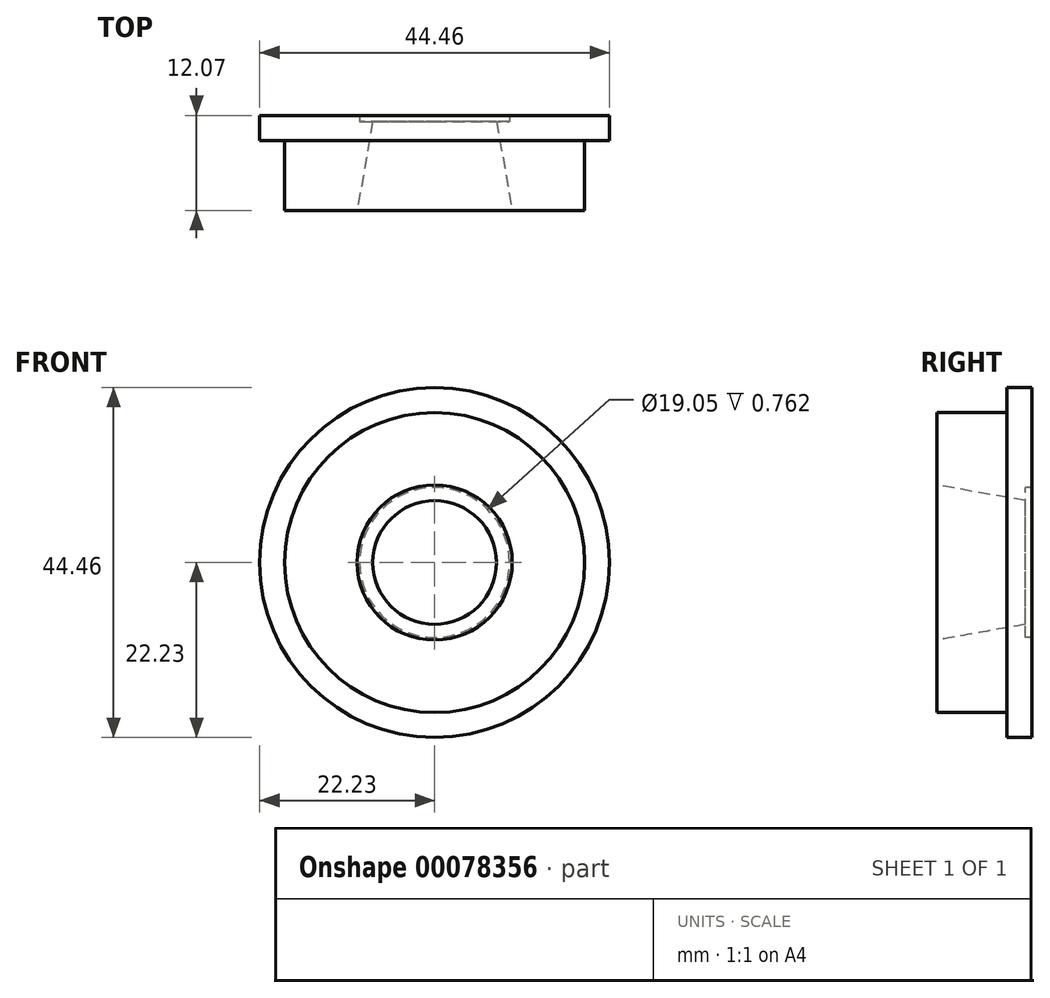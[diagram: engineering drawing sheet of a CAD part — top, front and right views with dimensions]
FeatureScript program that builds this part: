
annotation { "Feature Type Name" : "Feature", "Feature Type Description" : "" }
export const myFeature = defineFeature(function(context is Context, id is Id, definition is map)
    precondition{}
    {
        {
            var Q0;
            Q0=qCreatedBy(makeId("Right.planeOp"),FACE);
            var sketch = newSketch(context, id + "F0", { "sketchPlane" : qUnion([Q0])});
            skLineSegment(sketch, "E0", {"start": v(0, 9.85) * mm, "end": v(0, 19.05) * mm});
            skLineSegment(sketch, "E1", {"start": v(0, 19.05) * mm, "end": v(8.9, 19.05) * mm});
            skLineSegment(sketch, "E2", {"start": v(8.9, 19.05) * mm, "end": v(8.9, 22.23) * mm});
            skLineSegment(sketch, "E3", {"start": v(8.9, 22.23) * mm, "end": v(12.07, 22.23) * mm});
            skLineSegment(sketch, "E4", {"start": v(12.07, 22.23) * mm, "end": v(12.07, 9.53) * mm});
            skLineSegment(sketch, "E5", {"start": v(12.07, 9.53) * mm, "end": v(11.3, 9.53) * mm});
            skLineSegment(sketch, "E6", {"start": v(11.3, 7.86) * mm, "end": v(11.3, 9.53) * mm});
            skLineSegment(sketch, "E7", {"start": v(11.3, 7.86) * mm, "end": v(0, 9.85) * mm});
            skPoint(sketch, "E8.orphan", {"position": v(8.9, 0) * mm});
            skPoint(sketch, "E9.start.orphan", {"position": v(11.3, 0) * mm});
            skPoint(sketch, "E10.orphan", {"position": v(12.07, 0) * mm});
            skLineSegment(sketch, "E11", {"start": v(0, 0) * mm, "end": v(17.13, 0) * mm, "construction": true});
            skSolve(sketch);
        }
        {
            var Q0;
            Q0=makeQuery(id+"F0.imprint","IMPRINT",FACE,{"disambiguationData":[TD([[makeQuery(id+"F0.imprint","IMPRINT",EDGE,{"derivedFrom":sQuery(id+"F0.wireOp",EDGE,"E0")}),-1.0]])]});
            var Q1;
            Q1=sQuery(id+"F0.wireOp",EDGE,"E7");
            var Q2;
            Q2=sQuery(id+"F0.wireOp",EDGE,"E0");
            var Q3;
            Q3=sQuery(id+"F0.wireOp",EDGE,"E1");
            var Q4;
            Q4=sQuery(id+"F0.wireOp",EDGE,"E2");
            var Q5;
            Q5=sQuery(id+"F0.wireOp",EDGE,"E3");
            var Q6;
            Q6=sQuery(id+"F0.wireOp",EDGE,"E4");
            var Q7;
            Q7=sQuery(id+"F0.wireOp",EDGE,"E5");
            var Q8;
            Q8=sQuery(id+"F0.wireOp",EDGE,"E6");
            var Q9;
            Q9=sQuery(id+"F0.wireOp",EDGE,"E11");
            revolve(context, id + "F1", {"entities" : qUnion([Q0]), "surfaceEntities" : qUnion([Q1, Q2, Q3, Q4, Q5, Q6, Q7, Q8]), "axis" : qUnion([Q9]), "revolveType" : RevolveType.FULL});
        }
    });
